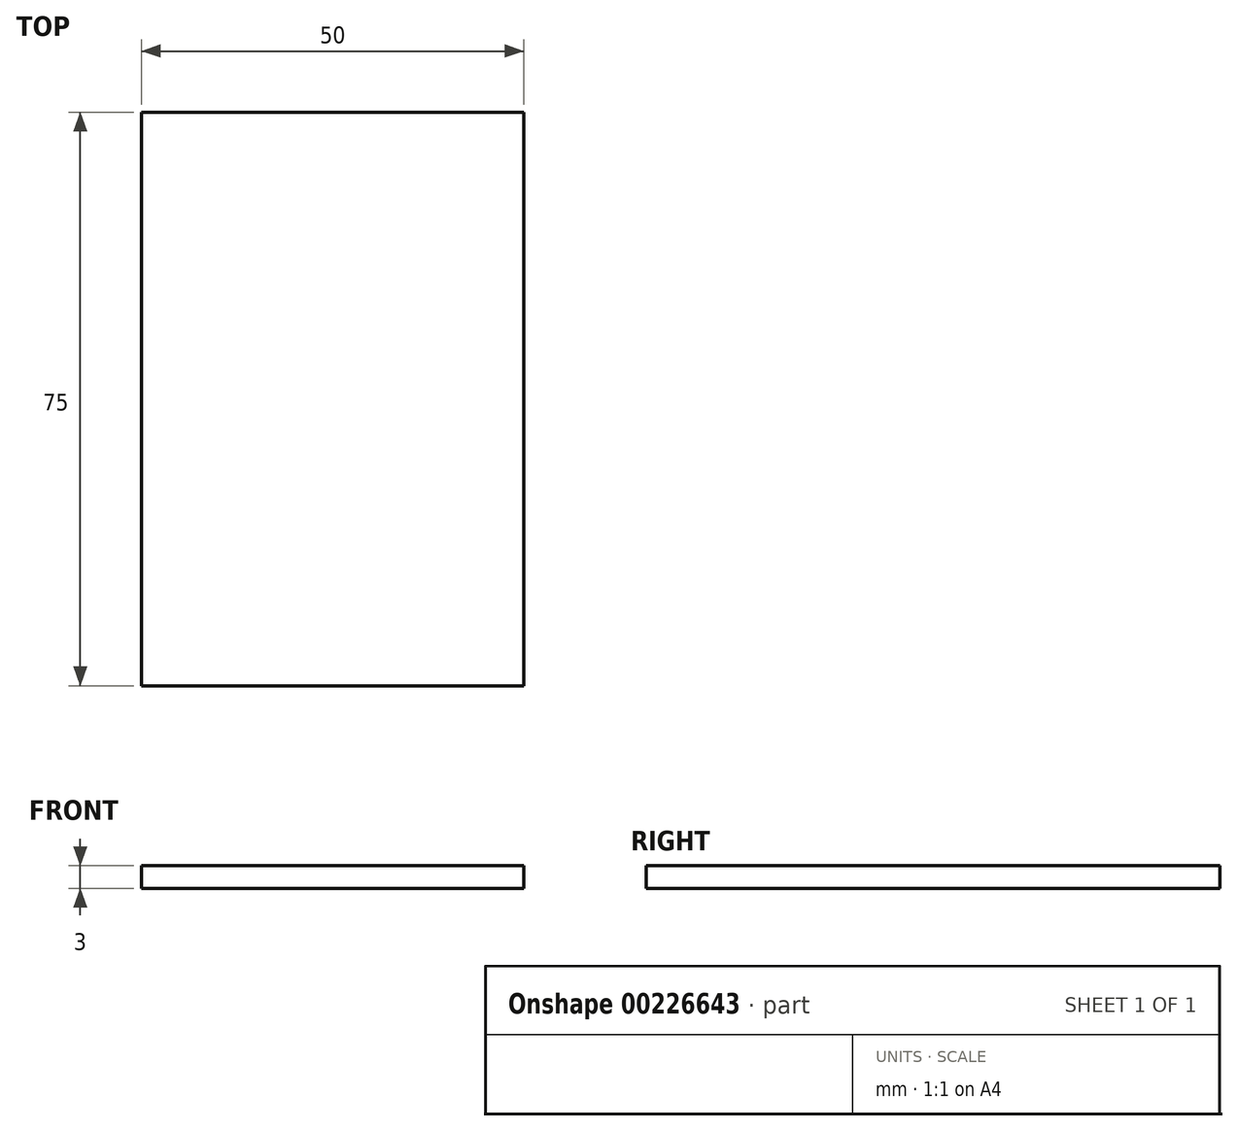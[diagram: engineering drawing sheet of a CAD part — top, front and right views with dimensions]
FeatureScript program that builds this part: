
annotation { "Feature Type Name" : "Feature", "Feature Type Description" : "" }
export const myFeature = defineFeature(function(context is Context, id is Id, definition is map)
    precondition{}
    {
        {
            var Q0;
            Q0=qCreatedBy(makeId("Top.planeOp"),FACE);
            var sketch = newSketch(context, id + "F0", { "sketchPlane" : qUnion([Q0])});
            skLineSegment(sketch, "E0.bottom", {"start": v(130, -40) * mm, "end": v(-130, -40) * mm});
            skLineSegment(sketch, "E0.top", {"start": v(130, 40) * mm, "end": v(-130, 40) * mm});
            skLineSegment(sketch, "E0.left", {"start": v(130, -40) * mm, "end": v(130, 40) * mm});
            skLineSegment(sketch, "E0.right", {"start": v(-130, -40) * mm, "end": v(-130, 40) * mm});
            skPoint(sketch, "E0.middle", {"position": v(0, 0) * mm});
            skLineSegment(sketch, "E1.bottom", {"start": v(-74.93, -37.5) * mm, "end": v(-124.93, -37.5) * mm});
            skLineSegment(sketch, "E1.top", {"start": v(-74.93, 37.5) * mm, "end": v(-124.93, 37.5) * mm});
            skLineSegment(sketch, "E1.left", {"start": v(-74.93, -37.5) * mm, "end": v(-74.93, 37.5) * mm});
            skLineSegment(sketch, "E1.right", {"start": v(-124.93, -37.5) * mm, "end": v(-124.93, 37.5) * mm});
            skPoint(sketch, "E1.middle", {"position": v(-99.93, 0) * mm});
            skSolve(sketch);
        }
        {
            var Q0;
            Q0=makeQuery(id+"F0.imprint","IMPRINT",FACE,{"disambiguationData":[TD([[makeQuery(id+"F0.imprint","IMPRINT",EDGE,{"derivedFrom":sQuery(id+"F0.wireOp",EDGE,"E1.bottom")}),-1.0]])]});
            extrude(context, id + "F1", {"entities" : qUnion([Q0]), "depth" : 3 * mm});
        }
    });
